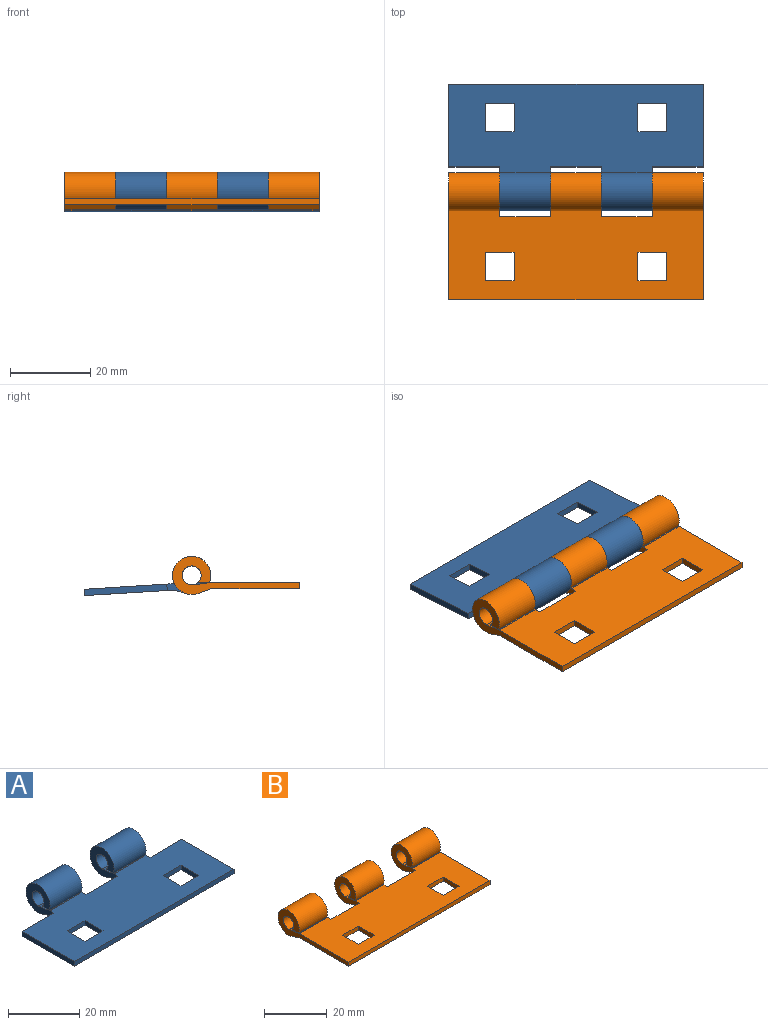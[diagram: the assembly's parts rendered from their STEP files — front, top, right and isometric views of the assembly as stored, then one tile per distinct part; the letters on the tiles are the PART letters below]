
ASSEMBLY  parts=2 mates=1
PART A: 30 faces, bbox 63.5x31.7x9.5 mm
  f0: plane 63.5x22.23mm, normal (0,0,1), area 1249.4mm2, adj f2,f3,f12,f13,f14,f15,f16,f17
  f1: plane 63.5x22.23mm, normal (0,0,-1), area 1249.4mm2, adj f4,f5,f12,f13,f14,f15,f16,f17
  f2: plane 12.7x4.44mm, normal (0,0.13,0.99), area 56.9mm2, adj f0,f10,f19,f21
  f3: plane 12.7x4.44mm, normal (0,0.13,0.99), area 56.9mm2, adj f0,f11,f16,f17
  f4: plane 12.7x3.14mm, normal (0,-0.34,-0.94), area 42.4mm2, adj f1,f6,f19,f21
  f5: plane 12.7x3.14mm, normal (0,-0.34,-0.94), area 42.4mm2, adj f1,f7,f16,f17
  f6: cylinder r=4.76mm len=12.7mm, axis (-1,0,0), area 328.9mm2, adj f4,f8,f19,f21
  f7: cylinder r=4.76mm len=12.7mm, axis (-1,0,0), area 328.9mm2, adj f5,f9,f16,f17
  f8: plane 12.7x2.84mm, normal (0,0,-1), area 36mm2, adj f6,f10,f19,f21
  f9: plane 12.7x2.84mm, normal (0,0,-1), area 36mm2, adj f7,f11,f16,f17
  f10: cylinder r=2.37mm len=12.7mm, axis (-1,0,0), area 171.4mm2, adj f2,f8,f19,f21
  f11: cylinder r=2.37mm len=12.7mm, axis (-1,0,0), area 171.4mm2, adj f3,f9,f16,f17
  f12: plane 20.65x1.59mm, normal (1,0,0), area 32.8mm2, adj f0,f1,f14,f20
  f13: plane 20.65x1.59mm, normal (-1,0,0), area 32.8mm2, adj f0,f1,f14,f15
  f14: plane 63.5x1.59mm, normal (0,-1,0), area 100.8mm2, adj f0,f1,f12,f13
  f15: plane 12.7x1.59mm, normal (0,1,0), area 20.2mm2, adj f0,f1,f13,f16
  f16: plane 11.09x9.53mm, normal (-1,0,0), area 57mm2, adj f0,f1,f3,f5,f7,f9,f11,f15
  f17: plane 11.09x9.53mm, normal (1,0,0), area 57mm2, adj f0,f1,f3,f5,f7,f9,f11,f18
  f18: plane 12.7x1.59mm, normal (0,1,0), area 20.2mm2, adj f0,f1,f17,f19
  f19: plane 11.09x9.53mm, normal (-1,0,0), area 57mm2, adj f0,f1,f2,f4,f6,f8,f10,f18
  f20: plane 12.7x1.59mm, normal (0,1,0), area 20.2mm2, adj f0,f1,f12,f21
  f21: plane 11.09x9.53mm, normal (1,0,0), area 57mm2, adj f0,f1,f2,f4,f6,f8,f10,f20
  f22: plane 7.14x1.59mm, normal (0,1,0), area 11.3mm2, adj f0,f1,f23,f25
  f23: plane 7.14x1.59mm, normal (-1,0,0), area 11.3mm2, adj f0,f1,f22,f24
  f24: plane 7.14x1.59mm, normal (0,-1,0), area 11.3mm2, adj f0,f1,f23,f25
  f25: plane 7.14x1.59mm, normal (1,0,0), area 11.3mm2, adj f0,f1,f22,f24
  f26: plane 7.14x1.59mm, normal (0,1,0), area 11.3mm2, adj f0,f1,f27,f29
  f27: plane 7.14x1.59mm, normal (-1,0,0), area 11.3mm2, adj f0,f1,f26,f28
  f28: plane 7.14x1.59mm, normal (0,-1,0), area 11.3mm2, adj f0,f1,f27,f29
  f29: plane 7.14x1.59mm, normal (1,0,0), area 11.3mm2, adj f0,f1,f26,f28
PART B: 34 faces, bbox 63.5x31.7x9.5 mm
  f0: plane 63.5x22.23mm, normal (0,0,-1), area 1269.4mm2, adj f2,f3,f12,f17,f18,f19,f20,f21
  f1: plane 63.5x22.23mm, normal (0,0,1), area 1269.4mm2, adj f10,f11,f16,f17,f18,f19,f20,f21
  f2: plane 12.7x3.14mm, normal (0,-0.34,-0.94), area 42.4mm2, adj f0,f4,f21,f25
  f3: plane 12.7x3.14mm, normal (0,-0.34,-0.94), area 42.4mm2, adj f0,f5,f19,f22
  f4: cylinder r=4.76mm len=12.7mm, axis (-1,0,0), area 328.9mm2, adj f2,f6,f21,f25
  f5: cylinder r=4.76mm len=12.7mm, axis (-1,0,0), area 328.9mm2, adj f3,f7,f19,f22
  f6: plane 12.7x2.84mm, normal (0,0,-1), area 36mm2, adj f4,f8,f21,f25
  f7: plane 12.7x2.84mm, normal (0,0,-1), area 36mm2, adj f5,f9,f19,f22
  f8: cylinder r=2.37mm len=12.7mm, axis (-1,0,0), area 171.4mm2, adj f6,f10,f21,f25
  f9: cylinder r=2.37mm len=12.7mm, axis (-1,0,0), area 171.4mm2, adj f7,f11,f19,f22
  f10: plane 12.7x4.44mm, normal (0,0.13,0.99), area 56.9mm2, adj f1,f8,f21,f25
  f11: plane 12.7x4.44mm, normal (0,0.13,0.99), area 56.9mm2, adj f1,f9,f19,f22
  f12: plane 12.7x3.14mm, normal (0,-0.34,-0.94), area 42.4mm2, adj f0,f13,f18,f24
  f13: cylinder r=4.76mm len=12.7mm, axis (-1,0,0), area 328.9mm2, adj f12,f14,f18,f24
  f14: plane 12.7x2.84mm, normal (0,0,-1), area 36mm2, adj f13,f15,f18,f24
  f15: cylinder r=2.37mm len=12.7mm, axis (-1,0,0), area 171.4mm2, adj f14,f16,f18,f24
  f16: plane 12.7x4.44mm, normal (0,0.13,0.99), area 56.9mm2, adj f1,f15,f18,f24
  f17: plane 63.5x1.59mm, normal (0,-1,0), area 100.8mm2, adj f0,f1,f18,f19
  f18: plane 31.74x9.53mm, normal (1,0,0), area 89.8mm2, adj f0,f1,f12,f13,f14,f15,f16,f17
  f19: plane 31.74x9.53mm, normal (-1,0,0), area 89.8mm2, adj f0,f1,f3,f5,f7,f9,f11,f17
  f20: plane 12.7x1.59mm, normal (0,1,0), area 20.2mm2, adj f0,f1,f21,f22
  f21: plane 11.09x9.53mm, normal (-1,0,0), area 57mm2, adj f0,f1,f2,f4,f6,f8,f10,f20
  f22: plane 11.09x9.53mm, normal (1,0,0), area 57mm2, adj f0,f1,f3,f5,f7,f9,f11,f20
  f23: plane 12.7x1.59mm, normal (0,1,0), area 20.2mm2, adj f0,f1,f24,f25
  f24: plane 11.09x9.53mm, normal (-1,0,0), area 57mm2, adj f0,f1,f12,f13,f14,f15,f16,f23
  f25: plane 11.09x9.53mm, normal (1,0,0), area 57mm2, adj f0,f1,f2,f4,f6,f8,f10,f23
  f26: plane 7.14x1.59mm, normal (0,1,0), area 11.3mm2, adj f0,f1,f27,f29
  f27: plane 7.14x1.59mm, normal (-1,0,0), area 11.3mm2, adj f0,f1,f26,f28
  f28: plane 7.14x1.59mm, normal (0,-1,0), area 11.3mm2, adj f0,f1,f27,f29
  f29: plane 7.14x1.59mm, normal (1,0,0), area 11.3mm2, adj f0,f1,f26,f28
  f30: plane 7.14x1.59mm, normal (0,1,0), area 11.3mm2, adj f0,f1,f31,f33
  f31: plane 7.14x1.59mm, normal (-1,0,0), area 11.3mm2, adj f0,f1,f30,f32
  f32: plane 7.14x1.59mm, normal (0,-1,0), area 11.3mm2, adj f0,f1,f31,f33
  f33: plane 7.14x1.59mm, normal (1,0,0), area 11.3mm2, adj f0,f1,f30,f32
PLACE A rot(axis=(0,0.03,1),180deg) t=(-68.31,73.4,-28.1)mm
PLACE B rot(axis=(-1,0,0),0deg) t=(-131.81,64.02,-27.8)mm fixed
MATE revolute A.f6 <-> B.f4  axis (-1,0,0) through (-93.71,68.77,-26.03)mm
